# Revit family: SALINA 215x145x10
name_source: partatom
category: Plumbing Fixtures
revit_build: Autodesk Revit 2018 (Build: 20170223_1515(x64)
units: mm (PartAtom-declared; Revit-internal decimal feet)

## family parameters
Always vertical = Yes
Cut with Voids When Loaded = No
OmniClass Number = 23.45.00.00
OmniClass Title = Sanitary, Laundry, and Cleaning Equipment
Part Type = Normal
Room Calculation Point = No
Round Connector Dimension = Use Diameter
Shared = No
Work Plane-Based = No

## types (5) — shared parameters
BIM object developer = www.concepsysbim.com
CONTROL_Actuation type = Pneumatique
CONTROL_Brief description = Plaque de commande pneumatique en abs
CONTROL_Height = 145 mm  [stored 0.475722 ft]
CONTROL_Length = 215 mm
CONTROL_Material = ABS
CONTROL_Model = SALINA
CONTROL_Product data url = https://www.regiplast.fr
CONTROL_Type of flush = Double-Débit
CONTROL_Type/function = Plaque de Commande pour réservoir à encastrer
CONTROL_Width = 10 mm  [stored 0.0328084 ft]
Description = Plaque de commande pneumatique en abs
URL = https://www.regiplast.fr

## per-type parameters (varying)
| type | CONTROL_Model Series | CONTROL_Model code/ref |
| Pneumatique_Blanc | Blanc | 1622B |
| Pneumatique_Chromée | Chromée | 1622C |
| Pneumatique_Chromée Mate | Chromée Mate | 1622M |
| Pneumatique_Noire soft | Noire soft | 1622NC |
| Pneumatique_Noire soft Mate | Noire soft Mate | 1622NCM |

note: [stored X ft] marks values corroborated as IEEE doubles in the binary element streams (Revit-internal decimal feet)

## geometry (parser evidence)
native form markers: Sweep x5
no freeform markers — native parametric forms only
